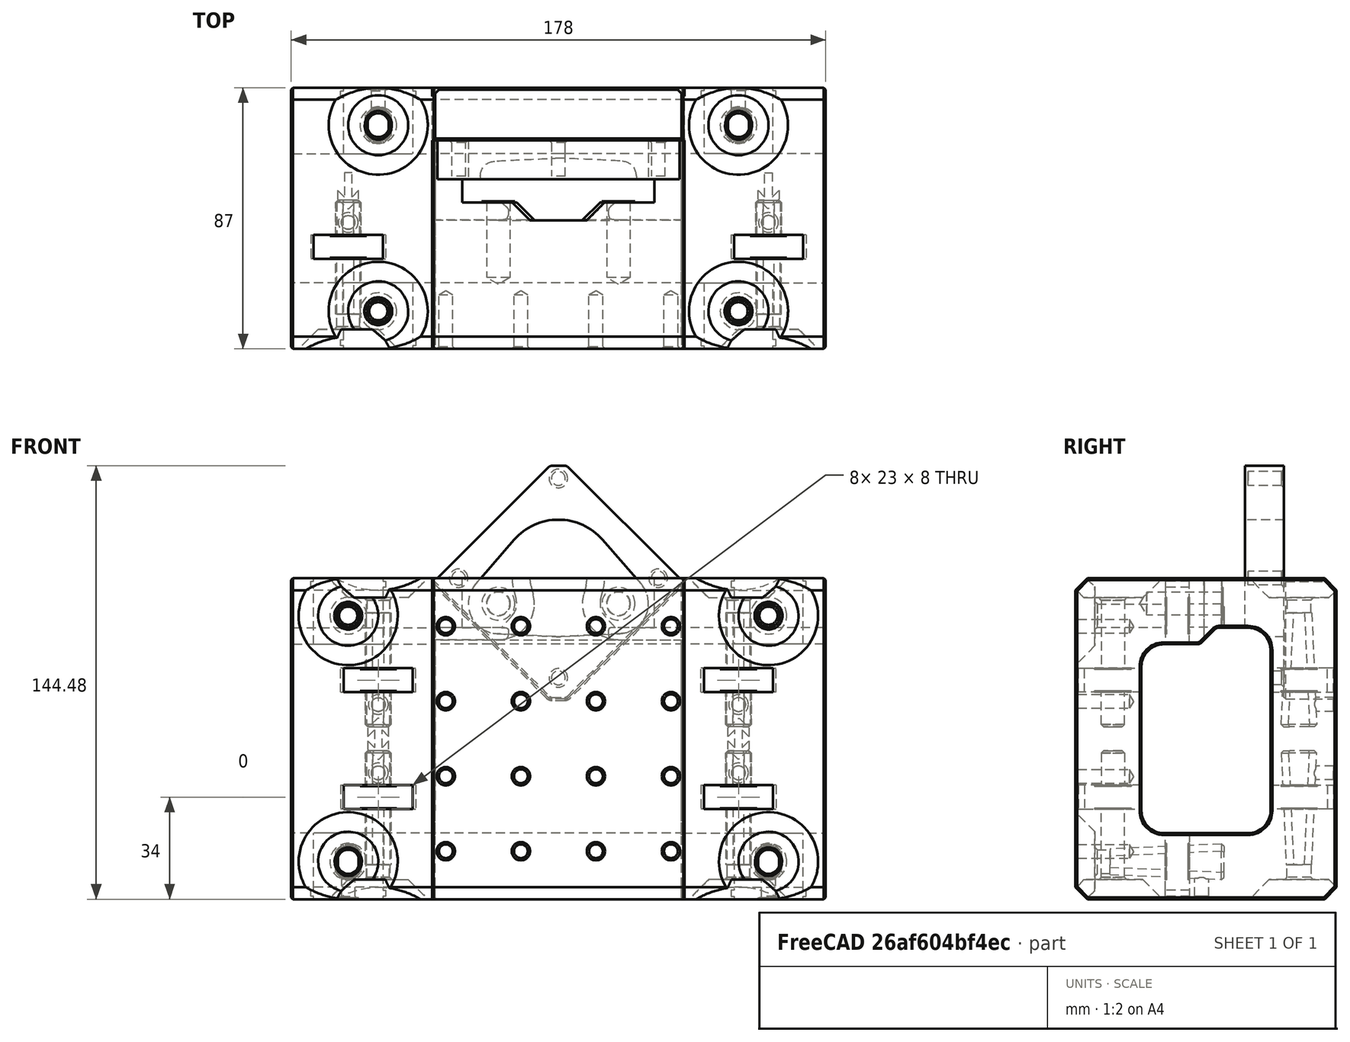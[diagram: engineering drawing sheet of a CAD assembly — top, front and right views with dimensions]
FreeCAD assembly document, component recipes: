
FREECAD ASSEMBLY — COMPONENT RECIPES ("Fabricatable-Axis-6.01-60mmx40mm-tube-version-Belt-drive-assembly")

This assembly document has 4 components, labeled P0..P3 below (a component is one placed body or linked part). 2 of them carry a construction recipe — the FreeCAD feature program that regenerates the part from scratch, quoted from this document or its linked companion documents; the rest are supplied as boundary geometry only. No exploded tour is included for this assembly.
COMPONENT P0 — recipe-attached ("Bearing ring - with all booleans", a linked part whose construction recipe lives in a companion FreeCAD document of the same project; that document's serialized recipe follows).
Construction recipe (the companion document, serialized — sketch geometry with constraints, then the solid features built on it; lengths are millimeters unless a unit is written):

FCSTD DOCUMENT  (FreeCAD 1.0R38641 +678 (Git))
Label: Fabricatable-Axis-6.01-60mmx40mm-tube-version-Bearing-ring
License: Creative Commons Attribution-ShareAlike 4.0
LicenseURL: https://creativecommons.org/licenses/by-sa/4.0/
objects: Part::FeaturePython×17, Sketcher::SketchObject×16, PartDesign::Pad×14, PartDesign::Body×9, PartDesign::Chamfer×7, PartDesign::Fillet×4, Part::Cut×3, App::Part×2, PartDesign::Pocket×2, Part::MultiFuse×2, Part::Compound×2, App::VarSet×1, PartDesign::Thickness×1, PartDesign::LinearPattern×1, PartDesign::FeatureBase×1
note: 153 computed .brp shape members not serialized (recipe doc carries the construction recipe); baked Part::Feature solids carry a one-line shape summary decoded from their .brp

FEATURE [App::VarSet] VarSet
  Attachment_hole_distance_from_edge = 8
  Attachment_hole_self_tap_diameter = 4.6
  Attachment_hole_spacing_horizontal = 60
  Attachment_hole_spacing_vertical = 80
  Bearing_axel_screw_oval_hole_depth = 5
  Bearing_axle_screw_diameter = 8
  Bearing_axle_screw_diameter_loose_diamter = 8.5
  Bearing_axle_screw_diameter_oval_selftap_diameter = 7.5
  Bearing_axle_screw_head_pocket_depth = 6.5
  Bearing_axle_screw_head_pocket_diamter = 20
  Bearing_axle_screw_length = 40
  Bearing_axle_screw_selftap_diameter = 7.7
  Bearing_distance_from_edge = 8
  Bearing_distance_from_fillet = 1
  Bearing_id = 8
  Bearing_od = 22
  Bearing_slot_width_margin = 1
  Bearing_tuning_screw_selftap_diameter = 4.6
  Bearing_washer_protrusion = 0.36
  Bearing_width = 7
  Carriage_to_bearing_top_clearance = 1.5
  Carriage_to_tube_clearance = 1.5
  Drive_chain_slot_height = 7
  Drive_chain_slot_width = 18
  Pivot_joint_spacer_thickness = 1.2
  Screw_offset = 2
  Tube_fillet_radius = 6
  Tube_height = 60
  Tube_thickness = 3
  Tube_width = 40
  Tuning_range_bearing = 2
FEATURE [Sketcher::SketchObject] Sketch
  ArcFitTolerance = 1e-06
  AttachmentSupport = -> [YZ_Plane]
  FullyConstrained = true
  MakeInternals = false
  MapMode = 5
  Placement = pos=(0,0,0) rot=(0.57735,0.57735,0.57735;2.0944rad)
  expr: .Constraints.beamheight = VarSet.Tube_height
  expr: .Constraints.beamwidth = VarSet.Tube_width
  sketch-geometry (4):
    g0: LineSegment StartX=-20 StartY=-30 StartZ=0 EndX=20 EndY=-30 EndZ=0
    g1: LineSegment StartX=20 StartY=-30 StartZ=0 EndX=20 EndY=30 EndZ=0
    g2: LineSegment StartX=20 StartY=30 StartZ=0 EndX=-20 EndY=30 EndZ=0
    g3: LineSegment StartX=-20 StartY=30 StartZ=0 EndX=-20 EndY=-30 EndZ=0
  constraints (10):
    c: Horizontal(g2)
    c: Vertical(g3)
    c: Distance(g1,g3) = 40  'beamwidth'
    c: Distance(g0,g2) = 60  'beamheight'
    c: Coincident(g0,g1)
    c: Coincident(g2,g1)
    c: Coincident(g3,g0)
    c: Coincident(g2,g3)
    c: Symmetric(g0,g1,g-1)
    c: Symmetric(g0,g0,g-2)
FEATURE [PartDesign::Pad] Pad
  Direction = (1,0,0)
  Length = 250
  Length2 = 10
  Midplane = true
  Placement = pos=(0,0,0) rot=(1,1,1;2.0944rad)
  Profile = -> Sketch
  ReferenceAxis = -> Sketch [N_Axis]
  Refine = true
  Reversed = true
  Suppressed = false
  Type = 0
FEATURE [PartDesign::Fillet] Fillet
  Base = -> Pad [Edge5,Edge2,Edge8,Edge1]
  BaseFeature = -> Pad
  Placement = pos=(0,0,0) rot=(1,1,1;2.0944rad)
  Radius = 6
  Refine = true
  SupportTransform = false
  Suppressed = false
  UseAllEdges = false
  expr: Radius = VarSet.Tube_fillet_radius
FEATURE [PartDesign::Thickness] Thickness
  Base = -> Fillet [Face2,Face5]
  BaseFeature = -> Fillet
  Intersection = false
  Join = 0
  Mode = 0
  Refine = true
  Reversed = true
  SupportTransform = false
  Suppressed = false
  Value = 3
  expr: Value = VarSet.Tube_thickness
FEATURE [PartDesign::Body] Body  label="Steel tube"
  AllowCompound = false
  Group = -> [Sketch,Pad,Fillet,Thickness]
  Origin = -> Origin
  Tip = -> Thickness
FEATURE [Sketcher::SketchObject] Sketch002
  ArcFitTolerance = 1e-06
  AttachmentSupport = -> [XY_Plane001]
  FullyConstrained = true
  MakeInternals = false
  MapMode = 5
  expr: Constraints[2] = VarSet.Bearing_od
  expr: Constraints[3] = VarSet.Bearing_id
  sketch-geometry (2):
    g0: Circle CenterX=0 CenterY=0 CenterZ=0 NormalX=0 NormalY=0 NormalZ=1 AngleXU=0 Radius=11
    g1: Circle CenterX=0 CenterY=0 CenterZ=0 NormalX=0 NormalY=0 NormalZ=1 AngleXU=0 Radius=4
  constraints (4):
    c: Coincident(g0,g-1)
    c: Coincident(g1,g0)
    c: Diameter(g0) = 22
    c: Diameter(g1) = 8
FEATURE [PartDesign::Pad] Pad001
  Direction = (0,0,1)
  Length = 7
  Length2 = 10
  Midplane = true
  Profile = -> Sketch002
  ReferenceAxis = -> Sketch002 [N_Axis]
  Refine = true
  Suppressed = false
  Type = 0
  expr: Length = VarSet.Bearing_width
FEATURE [Sketcher::SketchObject] Sketch003
  ArcFitTolerance = 1e-06
  AttachmentSupport = -> [YZ_Plane006]
  FullyConstrained = true
  MakeInternals = false
  MapMode = 5
  Placement = pos=(0,0,0) rot=(0.57735,0.57735,0.57735;2.0944rad)
  expr: .Constraints.y = VarSet.Tube_width / 2 + VarSet.Carriage_to_tube_clearance
  expr: .Constraints.z = VarSet.Tube_height / 2 + VarSet.Carriage_to_tube_clearance
  expr: Constraints[22] = VarSet.Tube_height / 2 + VarSet.Carriage_to_bearing_top_clearance + VarSet.Bearing_od
  expr: Constraints[23] = VarSet.Tube_width / 2 + VarSet.Carriage_to_bearing_top_clearance + VarSet.Bearing_od
  sketch-geometry (10):
    g0: LineSegment StartX=21.5 StartY=-31.5 StartZ=0 EndX=21.5 EndY=31.5 EndZ=0
    g1: LineSegment StartX=21.5 StartY=31.5 StartZ=0 EndX=-21.5 EndY=31.5 EndZ=0
    g2: LineSegment StartX=-21.5 StartY=31.5 StartZ=0 EndX=-21.5 EndY=-31.5 EndZ=0
    g3: LineSegment StartX=-21.5 StartY=-31.5 StartZ=0 EndX=21.5 EndY=-31.5 EndZ=0
    g4: GeomPoint [constr] X=0 Y=0 Z=0
    g5: LineSegment StartX=43.5 StartY=-53.5 StartZ=0 EndX=43.5 EndY=53.5 EndZ=0
    g6: LineSegment StartX=43.5 StartY=53.5 StartZ=0 EndX=-43.5 EndY=53.5 EndZ=0
    g7: LineSegment StartX=-43.5 StartY=53.5 StartZ=0 EndX=-43.5 EndY=-53.5 EndZ=0
    g8: LineSegment StartX=-43.5 StartY=-53.5 StartZ=0 EndX=43.5 EndY=-53.5 EndZ=0
    g9: GeomPoint [constr] X=0 Y=0 Z=0
  constraints (24):
    c: Coincident(g0,g1)
    c: Coincident(g1,g2)
    c: Coincident(g2,g3)
    c: Coincident(g3,g0)
    c: Vertical(g0)
    c: Vertical(g2)
    c: Horizontal(g1)
    c: Horizontal(g3)
    c: Symmetric(g2,g0,g4)
    c: Coincident(g4,g-1)
    c: Coincident(g5,g6)
    c: Coincident(g6,g7)
    c: Coincident(g7,g8)
    c: Coincident(g8,g5)
    c: Vertical(g5)
    c: Vertical(g7)
    c: Horizontal(g6)
    c: Horizontal(g8)
    c: Symmetric(g7,g5,g9)
    c: Coincident(g9,g4)
    c: DistanceY(g-1,g0) = 31.5  'z'
    c: DistanceX(g-2,g0) = 21.5  'y'
    c: DistanceY(g-1,g5) = 53.5
    c: DistanceX(g-2,g5) = 43.5
FEATURE [PartDesign::Fillet] Fillet001
  Base = -> Pad001 [Face3,Face4]
  BaseFeature = -> Pad001
  Radius = 0.5
  Refine = true
  SupportTransform = false
  Suppressed = false
  UseAllEdges = false
FEATURE [PartDesign::Body] Body001  label="Bearing"
  AllowCompound = false
  Group = -> [Sketch002,Pad001,Fillet001]
  Origin = -> Origin001
  Tip = -> Fillet001
FEATURE [Part::FeaturePython] Clone  label="Bearing001"  # Draft clone (typed FeaturePython)
  AttacherType = Attacher::AttachEngine3D
  Fuse = false
  Objects = -> [Body001]
  Placement = pos=(-5,-31,-19.5) rot=(0,0,1;0rad)
  Scale = (1,1,1)
  expr: .Placement.Base.x = -VarSet.Bearing_axle_screw_diameter / 2 - VarSet.Screw_offset / 2
  expr: .Placement.Base.y = -VarSet.Tube_width / 2 - VarSet.Bearing_od / 2
  expr: .Placement.Base.z = -VarSet.Tube_height / 2 + VarSet.Tube_fillet_radius + VarSet.Bearing_width / 2 + VarSet.Bearing_distance_from_fillet
FEATURE [Part::FeaturePython] Clone001  label="Bearing002"  # Draft clone (typed FeaturePython)
  AttacherType = Attacher::AttachEngine3D
  Fuse = false
  Objects = -> [Body001]
  Placement = pos=(-5,-31,19.5) rot=(0,0,1;0rad)
  Scale = (1,1,1)
  expr: .Placement.Base.x = <<Bearing001>>.Placement.Base.x
  expr: .Placement.Base.y = <<Bearing001>>.Placement.Base.y
  expr: .Placement.Base.z = -<<Bearing001>>.Placement.Base.z
FEATURE [Part::FeaturePython] Clone002  label="Bearing003"  # Draft clone (typed FeaturePython)
  AttacherType = Attacher::AttachEngine3D
  Fuse = false
  Objects = -> [Body001]
  Placement = pos=(-5,31,-19.5) rot=(0,0,1;0rad)
  Scale = (1,1,1)
  expr: .Placement.Base.x = <<Bearing001>>.Placement.Base.x
  expr: .Placement.Base.y = -<<Bearing001>>.Placement.Base.y
  expr: .Placement.Base.z = <<Bearing001>>.Placement.Base.z
FEATURE [Part::FeaturePython] Clone003  label="Bearing004"  # Draft clone (typed FeaturePython)
  AttacherType = Attacher::AttachEngine3D
  Fuse = false
  Objects = -> [Body001]
  Placement = pos=(-5,31,19.5) rot=(0,0,1;0rad)
  Scale = (1,1,1)
  expr: .Placement.Base.x = <<Bearing001>>.Placement.Base.x
  expr: .Placement.Base.y = -<<Bearing001>>.Placement.Base.y
  expr: .Placement.Base.z = -<<Bearing001>>.Placement.Base.z
FEATURE [Part::FeaturePython] Clone004  label="Bearing005"  # Draft clone (typed FeaturePython)
  AttacherType = Attacher::AttachEngine3D
  Fuse = false
  Objects = -> [Body001]
  Placement = pos=(5,-9.5,-41) rot=(1,0,0;1.5708rad)
  Scale = (1,1,1)
  expr: .Placement.Base.x = +VarSet.Bearing_axle_screw_diameter / 2 + VarSet.Screw_offset / 2
  expr: .Placement.Base.y = -VarSet.Tube_width / 2 + VarSet.Tube_fillet_radius + VarSet.Bearing_width / 2 + VarSet.Bearing_distance_from_fillet
  expr: .Placement.Base.z = -VarSet.Tube_height / 2 - VarSet.Bearing_od / 2
FEATURE [Part::FeaturePython] Clone005  label="Bearing006"  # Draft clone (typed FeaturePython)
  AttacherType = Attacher::AttachEngine3D
  Fuse = false
  Objects = -> [Body001]
  Placement = pos=(5,-9.5,41) rot=(1,0,0;4.71239rad)
  Scale = (1,1,1)
  expr: .Placement.Base.x = <<Bearing005>>.Placement.Base.x
  expr: .Placement.Base.y = -VarSet.Tube_width / 2 + VarSet.Tube_fillet_radius + VarSet.Bearing_width / 2 + VarSet.Bearing_distance_from_fillet
  expr: .Placement.Base.z = -<<Bearing005>>.Placement.Base.z
FEATURE [App::Part] Part001  label="Bearings"
  Group = -> [Body001,Clone,Clone001,Clone002,Clone003,Clone004,Clone005]
  Origin = -> Origin005
FEATURE [PartDesign::Pad] Pad002
  Direction = (1,0,0)
  Length = 48
  Length2 = 10
  Midplane = true
  Placement = pos=(0,0,0) rot=(1,1,1;2.0944rad)
  Profile = -> Sketch003
  ReferenceAxis = -> Sketch003 [N_Axis]
  Refine = true
  Suppressed = false
  Type = 0
  expr: Length = VarSet.Bearing_axle_screw_diameter + VarSet.Screw_offset + VarSet.Bearing_od + VarSet.Bearing_distance_from_edge * 2
FEATURE [Part::FeaturePython] Screw001  label="M5x10-Screw"  # WARN: FeaturePython — macro-defined, semantics opaque (R4)
  Diameter = 8
  Invert = false
  LeftHanded = false
  Length = 3
  LengthCustom = 10
  MatchOuter = false
  OffsetAngle = 0
  Placement = pos=(34,-50,30) rot=(1,0,0;1.5708rad)
  Thread = false
  Type = 70
FEATURE [Sketcher::SketchObject] Sketch005
  ArcFitTolerance = 1e-06
  AttachmentSupport = -> [XY_Plane008]
  FullyConstrained = true
  MakeInternals = false
  MapMode = 5
  expr: Constraints[11] = -VarSet.Bearing_od / 2 - VarSet.Carriage_to_bearing_top_clearance
  expr: Constraints[31] = VarSet.Bearing_slot_width_margin + VarSet.Bearing_od + 2 mm
  expr: Constraints[32] = -VarSet.Bearing_od / 2 - VarSet.Carriage_to_bearing_top_clearance + 1 mm
  expr: Constraints[33] = -VarSet.Bearing_od / 2 - VarSet.Carriage_to_bearing_top_clearance + 3 mm
  expr: Constraints[8] = VarSet.Bearing_slot_width_margin + VarSet.Bearing_od
  expr: Constraints[9] = VarSet.Bearing_od / 2
  sketch-geometry (13):
    g0: LineSegment StartX=11.5 StartY=-12.5 StartZ=0 EndX=11.5 EndY=11 EndZ=0
    g1: LineSegment StartX=11.5 StartY=11 StartZ=0 EndX=-11.5 EndY=11 EndZ=0
    g2: LineSegment StartX=-11.5 StartY=11 StartZ=0 EndX=-11.5 EndY=-12.5 EndZ=0
    g3: LineSegment StartX=-11.5 StartY=-12.5 StartZ=0 EndX=11.5 EndY=-12.5 EndZ=0
    g4: GeomPoint [constr] X=0 Y=0 Z=0
    g5: LineSegment StartX=11.5 StartY=-11.5 StartZ=0 EndX=12.5 EndY=-11.5 EndZ=0
    g6: LineSegment StartX=12.5 StartY=-11.5 StartZ=0 EndX=12.5 EndY=-9.5 EndZ=0
    g7: LineSegment StartX=12.5 StartY=-9.5 StartZ=0 EndX=11.5 EndY=-9.5 EndZ=0
    g8: LineSegment StartX=11.5 StartY=-9.5 StartZ=0 EndX=11.5 EndY=-11.5 EndZ=0
    g9: LineSegment StartX=-11.5 StartY=-9.5 StartZ=0 EndX=-12.5 EndY=-9.5 EndZ=0
    g10: LineSegment StartX=-12.5 StartY=-9.5 StartZ=0 EndX=-12.5 EndY=-11.5 EndZ=0
    g11: LineSegment StartX=-12.5 StartY=-11.5 StartZ=0 EndX=-11.5 EndY=-11.5 EndZ=0
    g12: LineSegment StartX=-11.5 StartY=-11.5 StartZ=0 EndX=-11.5 EndY=-9.5 EndZ=0
  constraints (34):
    c: Coincident(g0,g1)
    c: Coincident(g1,g2)
    c: Coincident(g2,g3)
    c: Coincident(g3,g0)
    c: Vertical(g0)
    c: Vertical(g2)
    c: Horizontal(g1)
    c: Coincident(g4,g-1)
    c: Distance(g3) = 23
    c: DistanceY(g-1,g0) = 11
    c: Symmetric(g0,g2,g-2)
    c: DistanceY(g-1,g0) = -12.5
    c: Coincident(g5,g6)
    c: Coincident(g6,g7)
    c: Coincident(g7,g8)
    c: Coincident(g8,g5)
    c: Horizontal(g5)
    c: Horizontal(g7)
    c: Vertical(g6)
    c: Vertical(g8)
    c: PointOnObject(g5,g0)
    c: Coincident(g9,g10)
    c: Coincident(g10,g11)
    c: Coincident(g11,g12)
    c: Coincident(g12,g9)
    c: Horizontal(g9)
    c: Horizontal(g11)
    c: Vertical(g10)
    c: Vertical(g12)
    c: Symmetric(g9,g7,g-2)
    c: Symmetric(g10,g5,g-2)
    c: Distance(g5,g10) = 25
    c: DistanceY(g-1,g5) = -11.5
    c: DistanceY(g-1,g6) = -9.5
FEATURE [Sketcher::SketchObject] Sketch006
  ArcFitTolerance = 1e-06
  AttachmentSupport = -> [YZ_Plane006]
  FullyConstrained = true
  MakeInternals = false
  MapMode = 5
  Placement = pos=(0,0,0) rot=(0.57735,0.57735,0.57735;2.0944rad)
  expr: Constraints[10] = Sketch003.Constraints.y - VarSet.Drive_chain_slot_width
  expr: Constraints[7] = Sketch003.Constraints.y
  expr: Constraints[8] = Sketch003.Constraints.z
  expr: Constraints[9] = VarSet.Tube_height / 2 + VarSet.Drive_chain_slot_height
  sketch-geometry (4):
    g0: LineSegment StartX=-2 StartY=31.5 StartZ=0 EndX=21.5 EndY=31.5 EndZ=0
    g1: LineSegment StartX=21.5 StartY=31.5 StartZ=0 EndX=21.5 EndY=37 EndZ=0
    g2: LineSegment StartX=21.5 StartY=37 StartZ=0 EndX=3.5 EndY=37 EndZ=0
    g3: LineSegment StartX=3.5 StartY=37 StartZ=0 EndX=-2 EndY=31.5 EndZ=0
  constraints (12):
    c: Coincident(g0,g1)
    c: Coincident(g1,g2)
    c: Coincident(g2,g3)
    c: Coincident(g3,g0)
    c: Horizontal(g0)
    c: Horizontal(g2)
    c: Vertical(g1)
    c: DistanceX(g-2,g0) = 21.5
    c: DistanceY(g-1,g0) = 31.5
    c: DistanceY(g-1,g1) = 37
    c: DistanceX(g-2,g2) = 3.5
    c: Angle(g-2,g3) = 2.35619
FEATURE [PartDesign::Pocket] Pocket
  BaseFeature = -> Pad002
  Direction = (-1,0,0)
  Length = 5
  Length2 = 5
  Midplane = true
  Placement = pos=(0,0,0) rot=(1,1,1;2.0944rad)
  Profile = -> Sketch006
  ReferenceAxis = -> Sketch006 [N_Axis]
  Refine = true
  Suppressed = false
  Type = 1
FEATURE [PartDesign::Fillet] Fillet006
  Base = -> Pocket [Edge26,Edge30,Edge29,Edge28]
  BaseFeature = -> Pocket
  Placement = pos=(0,0,0) rot=(1,1,1;2.0944rad)
  Radius = 7.5
  Refine = true
  SupportTransform = false
  Suppressed = false
  UseAllEdges = false
  expr: Radius = VarSet.Tube_fillet_radius + VarSet.Carriage_to_tube_clearance
FEATURE [PartDesign::Fillet] Fillet007
  Base = -> Fillet006 [Edge25,Edge29]
  BaseFeature = -> Fillet006
  Placement = pos=(0,0,0) rot=(1,1,1;2.0944rad)
  Radius = 2
  Refine = true
  SupportTransform = false
  Suppressed = false
  UseAllEdges = false
FEATURE [PartDesign::Chamfer] Chamfer
  Angle = 45
  Base = -> Fillet007 [Edge44,Edge46,Edge41,Edge42]
  BaseFeature = -> Fillet007
  ChamferType = 0
  FlipDirection = false
  Placement = pos=(0,0,0) rot=(1,1,1;2.0944rad)
  Refine = true
  Size = 4
  Size2 = 1
  SupportTransform = false
  Suppressed = false
  UseAllEdges = false
FEATURE [PartDesign::Pad] Pad004
  Direction = (0,0,1)
  Length = 8
  Length2 = 10
  Midplane = true
  Profile = -> Sketch005
  ReferenceAxis = -> Sketch005 [N_Axis]
  Refine = true
  Suppressed = false
  Type = 0
  expr: Length = VarSet.Bearing_width + VarSet.Bearing_slot_width_margin
FEATURE [Sketcher::SketchObject] Sketch007
  ArcFitTolerance = 1e-06
  AttachmentOffset = pos=(0,0,4) rot=(0,0,1;0rad)
  AttachmentSupport = -> [XY_Plane008]
  FullyConstrained = true
  MakeInternals = false
  MapMode = 5
  Placement = pos=(0,0,4) rot=(0,0,1;0rad)
  expr: .AttachmentOffset.Base.z = Pad004.Length / 2
  expr: Constraints[1] = VarSet.Bearing_od / 1.8
  sketch-geometry (1):
    g0: Circle CenterX=0 CenterY=0 CenterZ=0 NormalX=0 NormalY=0 NormalZ=1 AngleXU=0 Radius=6.11111
  constraints (2):
    c: Coincident(g0,g-1)
    c: Diameter(g0) = 12.2222
FEATURE [PartDesign::Pocket] Pocket001
  BaseFeature = -> Pad004
  Direction = (0,0,-1)
  Length = 0.36
  Length2 = 5
  Profile = -> Sketch007
  ReferenceAxis = -> Sketch007 [N_Axis]
  Refine = true
  Suppressed = false
  Type = 0
  expr: Length = VarSet.Bearing_washer_protrusion
FEATURE [PartDesign::LinearPattern] LinearPattern
  BaseFeature = -> Pocket001
  Direction = -> Z_Axis008
  Length = 7.64
  Mode = 0
  Occurrences = 2
  Offset = 7.64
  Originals = -> [Pocket001]
  Refine = true
  Reversed = true
  Suppressed = false
  TransformMode = 0
  expr: Length = Pad004.Length - Pocket001.Length
FEATURE [PartDesign::FeatureBase] Clone007
  BaseFeature = -> LinearPattern
  Suppressed = false
FEATURE [PartDesign::Body] Body005  label="Body for boolean - hole maker adjustable"
  AllowCompound = false
  Group = -> [Clone007]
  Origin = -> Origin009
  Tip = -> Clone007
FEATURE [Sketcher::SketchObject] Sketch008
  ArcFitTolerance = 1e-06
  AttachmentSupport = -> [XY_Plane008]
  FullyConstrained = true
  MakeInternals = false
  MapMode = 5
  expr: Constraints[1] = VarSet.Bearing_axle_screw_selftap_diameter
  sketch-geometry (1):
    g0: Circle CenterX=0 CenterY=0 CenterZ=0 NormalX=0 NormalY=0 NormalZ=1 AngleXU=0 Radius=3.85
  constraints (2):
    c: Coincident(g0,g-1)
    c: Diameter(g0) = 7.7
FEATURE [PartDesign::Pad] Pad005
  BaseFeature = -> LinearPattern
  Direction = (0,0,1)
  Length = 27.5
  Length2 = 10
  Profile = -> Sketch008
  ReferenceAxis = -> Sketch008 [N_Axis]
  Refine = true
  Suppressed = false
  Type = 0
  expr: Length = VarSet.Bearing_width / 2 + VarSet.Bearing_distance_from_fillet + VarSet.Tube_fillet_radius + VarSet.Bearing_od + VarSet.Carriage_to_bearing_top_clearance - VarSet.Bearing_axle_screw_head_pocket_depth
FEATURE [PartDesign::Pad] Pad006
  BaseFeature = -> Pad005
  Direction = (0,0,1)
  Length = 15.5
  Length2 = 10
  Profile = -> Sketch008
  ReferenceAxis = -> Sketch008 [N_Axis]
  Refine = true
  Reversed = true
  Suppressed = false
  Type = 0
  expr: Length = VarSet.Bearing_axle_screw_length + 3 mm - Pad005.Length
FEATURE [Sketcher::SketchObject] Sketch009
  ArcFitTolerance = 1e-06
  AttachmentSupport = -> [Pad006]
  FullyConstrained = true
  MakeInternals = false
  MapMode = 5
  Placement = pos=(0,0,27.5) rot=(0,0,1;0rad)
  expr: Constraints[1] = VarSet.Bearing_axle_screw_head_pocket_diamter
  sketch-geometry (1):
    g0: Circle CenterX=0 CenterY=0 CenterZ=0 NormalX=0 NormalY=0 NormalZ=1 AngleXU=0 Radius=10
  constraints (2):
    c: Coincident(g0,g-1)
    c: Diameter(g0) = 20
FEATURE [PartDesign::Pad] Pad007
  BaseFeature = -> Pad006
  Direction = (0,0,1)
  Length = 6.5
  Length2 = 10
  Profile = -> Sketch009
  ReferenceAxis = -> Sketch009 [N_Axis]
  Refine = true
  Suppressed = false
  TaperAngle = 45
  Type = 0
  expr: Length = VarSet.Bearing_axle_screw_head_pocket_depth
FEATURE [PartDesign::Chamfer] Chamfer002
  Angle = 45
  Base = -> Pad007 [Edge46,Edge48]
  BaseFeature = -> Pad007
  ChamferType = 0
  FlipDirection = false
  Refine = true
  Size = 0.8
  Size2 = 1
  SupportTransform = false
  Suppressed = false
  UseAllEdges = false
FEATURE [PartDesign::Chamfer] Chamfer003
  Angle = 45
  Base = -> Chamfer002 [Edge51,Edge3]
  BaseFeature = -> Chamfer002
  ChamferType = 0
  FlipDirection = false
  Refine = true
  Size = 0.3
  Size2 = 1
  SupportTransform = false
  Suppressed = false
  UseAllEdges = false
FEATURE [PartDesign::Body] Body004  label="Body - hole maker non adjustable"
  AllowCompound = false
  Group = -> [Sketch005,Pad004,Sketch007,Pocket001,LinearPattern,Sketch008,Pad005,Pad006,Sketch009,Pad007,Chamfer002,Chamfer003]
  Origin = -> Origin008
  Tip = -> Chamfer003
FEATURE [Part::FeaturePython] Clone006  label="Clone - hole maker non adjustable - for bearing002"  # Draft clone (typed FeaturePython)
  AttacherType = Attacher::AttachEngine3D
  Fuse = false
  Objects = -> [Body004]
  Placement = pos=(-5,-31,19.5) rot=(0,0,1;0rad)
  Scale = (1,1,1)
  expr: .Placement.Base.x = <<Bearing002>>.Placement.Base.x
  expr: .Placement.Base.y = <<Bearing002>>.Placement.Base.y
  expr: .Placement.Base.z = <<Bearing002>>.Placement.Base.z
FEATURE [Part::FeaturePython] Clone008  label="Clone - hole maker non adjustable - for bearing006"  # Draft clone (typed FeaturePython)
  AttacherType = Attacher::AttachEngine3D
  Fuse = false
  Objects = -> [Body004]
  Placement = pos=(5,-9.5,41) rot=(0,-0.707107,0.707107;3.14159rad)
  Scale = (1,1,1)
  expr: .Placement.Base.x = <<Bearing006>>.Placement.Base.x
  expr: .Placement.Base.y = <<Bearing006>>.Placement.Base.y
  expr: .Placement.Base.z = <<Bearing006>>.Placement.Base.z
FEATURE [Sketcher::SketchObject] Sketch013
  ArcFitTolerance = 1e-06
  AttachmentSupport = -> [YZ_Plane011]
  FullyConstrained = true
  MakeInternals = false
  MapMode = 5
  Placement = pos=(0,0,0) rot=(0.57735,0.57735,0.57735;2.0944rad)
  expr: .Constraints.z = Pad005.Length - VarSet.Bearing_axel_screw_oval_hole_depth
  expr: Constraints[12] = VarSet.Bearing_axle_screw_diameter_loose_diamter + VarSet.Tuning_range_bearing
  expr: Constraints[7] = -Pad006.Length
  expr: Constraints[8] = VarSet.Bearing_axle_screw_diameter_loose_diamter
  sketch-geometry (5):
    g0: LineSegment StartX=-4.25 StartY=22.5 StartZ=0 EndX=-5.93889 EndY=-15.5 EndZ=0
    g1: LineSegment StartX=-5.93889 StartY=-15.5 StartZ=0 EndX=5.93889 EndY=-15.5 EndZ=0
    g2: LineSegment StartX=5.93889 StartY=-15.5 StartZ=0 EndX=4.25 EndY=22.5 EndZ=0
    g3: LineSegment StartX=4.25 StartY=22.5 StartZ=0 EndX=-4.25 EndY=22.5 EndZ=0
    g4: LineSegment [constr] StartX=-5.25 StartY=0 StartZ=0 EndX=5.25 EndY=0 EndZ=0
  constraints (14):
    c: Coincident(g0,g1)
    c: Coincident(g1,g2)
    c: Coincident(g2,g3)
    c: Coincident(g3,g0)
    c: Symmetric(g2,g0,g-2)
    c: Symmetric(g0,g1,g-2)
    c: DistanceY(g-1,g2) = 22.5  'z'
    c: DistanceY(g-1,g1) = -15.5
    c: Distance(g3) = 8.5
    c: Distance(g1) = 11.8778
    c: PointOnObject(g4,g-1)
    c: Symmetric(g4,g4,g-2)
    c: Distance(g4) = 10.5
    c: PointOnObject(g4,g0)
FEATURE [PartDesign::Pad] Pad008
  Direction = (1,0,0)
  Length = 8.5
  Length2 = 10
  Midplane = true
  Placement = pos=(0,0,0) rot=(1,1,1;2.0944rad)
  Profile = -> Sketch013
  ReferenceAxis = -> Sketch013 [N_Axis]
  Refine = true
  Suppressed = false
  Type = 0
  expr: Length = VarSet.Bearing_axle_screw_diameter_loose_diamter
FEATURE [PartDesign::Chamfer] Chamfer004
  Angle = 45
  Base = -> Pad008 [Edge4,Edge3,Edge10,Edge9]
  BaseFeature = -> Pad008
  ChamferType = 0
  FlipDirection = false
  Placement = pos=(0,0,0) rot=(1,1,1;2.0944rad)
  Refine = true
  Size = 2.42857
  Size2 = 1
  SupportTransform = false
  Suppressed = false
  UseAllEdges = false
  expr: Size = VarSet.Bearing_axle_screw_diameter_loose_diamter / 3.5
FEATURE [PartDesign::Chamfer] Chamfer005
  Angle = 45
  Base = -> Chamfer004 [Face5]
  BaseFeature = -> Chamfer004
  ChamferType = 0
  FlipDirection = false
  Placement = pos=(0,0,0) rot=(1,1,1;2.0944rad)
  Refine = true
  Size = 0.8
  Size2 = 1
  SupportTransform = false
  Suppressed = false
  UseAllEdges = false
FEATURE [Sketcher::SketchObject] Sketch014
  ArcFitTolerance = 1e-06
  AttachmentOffset = pos=(0,0,22.5) rot=(0,0,1;0rad)
  AttachmentSupport = -> [XY_Plane011]
  FullyConstrained = false
  MakeInternals = false
  MapMode = 5
  Placement = pos=(0,0,22.5) rot=(0,0,1;0rad)
  expr: .AttachmentOffset.Base.z = Sketch013.Constraints.z
  expr: Constraints[5] = VarSet.Bearing_axle_screw_diameter
  expr: Constraints[6] = VarSet.Bearing_axle_screw_diameter_oval_selftap_diameter
  sketch-geometry (5):
    g0: Ellipse CenterX=0 CenterY=0 CenterZ=0 NormalX=0 NormalY=0 NormalZ=1 MajorRadius=4 MinorRadius=3.75 AngleXU=-1.5708
    g1: LineSegment [constr] StartX=1e-16 StartY=-4 StartZ=0 EndX=-1e-16 EndY=4 EndZ=0
    g2: LineSegment [constr] StartX=3.75 StartY=1e-16 StartZ=0 EndX=-3.75 EndY=-1e-16 EndZ=0
    g3: GeomPoint [constr] X=2e-16 Y=-1.39194 Z=0
    g4: GeomPoint [constr] X=0 Y=1.39194 Z=0
  constraints (4):
    c: InternalAlignment(g1-g4 -> g0) x4
    c: Coincident(g0,g-1)
    c: Distance(g1,g1) = 8
    c: Distance(g2,g2) = 7.5
FEATURE [PartDesign::Pad] Pad009
  BaseFeature = -> Chamfer005
  Direction = (0,0,1)
  Length = 5
  Length2 = 10
  Placement = pos=(0,0,0) rot=(1,1,1;2.0944rad)
  Profile = -> Sketch014
  ReferenceAxis = -> Sketch014 [N_Axis]
  Refine = true
  Suppressed = false
  Type = 0
  expr: Length = VarSet.Bearing_axel_screw_oval_hole_depth
FEATURE [Sketcher::SketchObject] Sketch015
  ArcFitTolerance = 1e-06
  AttachmentOffset = pos=(0,0,27.5) rot=(0,0,1;0rad)
  AttachmentSupport = -> [XY_Plane011]
  FullyConstrained = true
  MakeInternals = false
  MapMode = 5
  Placement = pos=(0,0,27.5) rot=(0,0,1;0rad)
  expr: .AttachmentOffset.Base.z = Sketch013.Constraints.z + VarSet.Bearing_axel_screw_oval_hole_depth
  expr: Constraints[1] = VarSet.Bearing_axle_screw_head_pocket_diamter
  sketch-geometry (1):
    g0: Circle CenterX=0 CenterY=0 CenterZ=0 NormalX=0 NormalY=0 NormalZ=1 AngleXU=0 Radius=10
  constraints (2):
    c: Coincident(g0,g-1)
    c: Diameter(g0) = 20
FEATURE [PartDesign::Pad] Pad010
  BaseFeature = -> Pad009
  Direction = (0,0,1)
  Length = 32.5
  Length2 = 10
  Placement = pos=(0,0,0) rot=(1,1,1;2.0944rad)
  Profile = -> Sketch015
  ReferenceAxis = -> Sketch015 [N_Axis]
  Refine = true
  Suppressed = false
  TaperAngle = 45
  Type = 0
  expr: Length = VarSet.Bearing_axle_screw_head_pocket_depth * 5
FEATURE [Sketcher::SketchObject] Sketch016
  ArcFitTolerance = 1e-06
  AttachmentSupport = -> [XZ_Plane011]
  FullyConstrained = true
  MakeInternals = false
  MapMode = 5
  Placement = pos=(0,0,0) rot=(1,0,0;1.5708rad)
  expr: .Constraints.z = -VarSet.Bearing_width / 2 - VarSet.Bearing_slot_width_margin / 2 - VarSet.Bearing_tuning_screw_selftap_diameter / 2 - 1.8 mm
  expr: Constraints[1] = VarSet.Bearing_tuning_screw_selftap_diameter
  sketch-geometry (1):
    g0: Circle CenterX=0 CenterY=-8.1 CenterZ=0 NormalX=0 NormalY=0 NormalZ=1 AngleXU=0 Radius=2.3
  constraints (3):
    c: PointOnObject(g0,g-2)
    c: Diameter(g0) = 4.6
    c: DistanceY(g-1,g0) = -8.1  'z'
FEATURE [PartDesign::Pad] Pad011
  BaseFeature = -> Pad010
  Direction = (0,-1,2e-16)
  Length = 11.5
  Length2 = 10
  Placement = pos=(0,0,0) rot=(1,1,1;2.0944rad)
  Profile = -> Sketch016
  ReferenceAxis = -> Sketch016 [N_Axis]
  Refine = true
  Suppressed = false
  Type = 0
  expr: Length = VarSet.Bearing_od / 2 + VarSet.Carriage_to_bearing_top_clearance - 1 mm
FEATURE [Part::FeaturePython] Clone012  label="Clone - hole maker non adjustable - for bearing001"  # Draft clone (typed FeaturePython)
  AttacherType = Attacher::AttachEngine3D
  Fuse = false
  Objects = -> [Body004]
  Placement = pos=(-5,-31,-19.5) rot=(0,1,0;3.14159rad)
  Scale = (1,1,1)
  expr: .Placement.Base.x = <<Bearing001>>.Placement.Base.x
  expr: .Placement.Base.y = <<Bearing001>>.Placement.Base.y
  expr: .Placement.Base.z = <<Bearing001>>.Placement.Base.z
FEATURE [Sketcher::SketchObject] Sketch017
  ArcFitTolerance = 1e-06
  AttachmentOffset = pos=(0,0,11.5) rot=(0,0,1;0rad)
  AttachmentSupport = -> [XZ_Plane011]
  FullyConstrained = true
  MakeInternals = false
  MapMode = 5
  Placement = pos=(0,-11.5,2.6e-15) rot=(1,0,0;1.5708rad)
  expr: .AttachmentOffset.Base.z = VarSet.Bearing_od / 2 + VarSet.Carriage_to_bearing_top_clearance - 1 mm
  expr: Constraints[0] = VarSet.Bearing_tuning_screw_selftap_diameter
  expr: Constraints[1] = Sketch016.Constraints.z
  sketch-geometry (1):
    g0: Circle CenterX=0 CenterY=-8.1 CenterZ=0 NormalX=0 NormalY=0 NormalZ=1 AngleXU=0 Radius=2.3
  constraints (3):
    c: Diameter(g0) = 4.6
    c: DistanceY(g-1,g0) = -8.1
    c: PointOnObject(g0,g-2)
FEATURE [PartDesign::Pad] Pad012
  BaseFeature = -> Pad011
  Direction = (0,-1,2e-16)
  Length = 1
  Length2 = 10
  Placement = pos=(0,0,0) rot=(1,1,1;2.0944rad)
  Profile = -> Sketch017
  ReferenceAxis = -> Sketch017 [N_Axis]
  Refine = true
  Suppressed = false
  TaperAngle = 45
  Type = 0
FEATURE [PartDesign::Chamfer] Chamfer006
  Angle = 45
  Base = -> Pad012 [Edge44]
  BaseFeature = -> Pad012
  ChamferType = 0
  FlipDirection = false
  Placement = pos=(0,0,0) rot=(1,1,1;2.0944rad)
  Refine = true
  Size = 0.8
  Size2 = 1
  SupportTransform = false
  Suppressed = false
  UseAllEdges = false
FEATURE [PartDesign::Body] Body007  label="Body for boolean - rotation hole"
  AllowCompound = false
  Group = -> [Sketch013,Pad008,Chamfer004,Chamfer005,Sketch014,Pad009,Sketch015,Pad010,Sketch016,Pad011,Sketch017,Pad012,Chamfer006]
  Origin = -> Origin011
  Tip = -> Chamfer006
FEATURE [Part::MultiFuse] Fusion001  label="Fusion - hole maker adjustable"
  Refine = true
  Shapes = -> [Body005,Body007]
FEATURE [Part::FeaturePython] Clone009  label="Clone - Hole maker adjustable - for bearing003"  # Draft clone (typed FeaturePython)
  AttacherType = Attacher::AttachEngine3D
  Fuse = false
  Objects = -> [Fusion001]
  Placement = pos=(-5,31,-19.5) rot=(1,0,0;3.14159rad)
  Scale = (1,1,1)
  expr: .Placement.Base.x = <<Bearing003>>.Placement.Base.x
  expr: .Placement.Base.y = <<Bearing003>>.Placement.Base.y
  expr: .Placement.Base.z = <<Bearing003>>.Placement.Base.z
FEATURE [Part::FeaturePython] Clone010  label="Clone - Hole maker adjustable - for bearing004"  # Draft clone (typed FeaturePython)
  AttacherType = Attacher::AttachEngine3D
  Fuse = false
  Objects = -> [Fusion001]
  Placement = pos=(-5,31,19.5) rot=(0,0,1;3.14159rad)
  Scale = (1,1,1)
  expr: .Placement.Base.x = <<Bearing004>>.Placement.Base.x
  expr: .Placement.Base.y = <<Bearing004>>.Placement.Base.y
  expr: .Placement.Base.z = <<Bearing004>>.Placement.Base.z
FEATURE [Part::FeaturePython] Clone011  label="Clone - Hole maker adjustable - for bearing005"  # Draft clone (typed FeaturePython)
  AttacherType = Attacher::AttachEngine3D
  Fuse = false
  Objects = -> [Fusion001]
  Placement = pos=(5,-9.5,-41) rot=(1,0,0;1.5708rad)
  Scale = (1,1,1)
  expr: .Placement.Base.x = <<Bearing005>>.Placement.Base.x
  expr: .Placement.Base.y = <<Bearing005>>.Placement.Base.y
  expr: .Placement.Base.z = <<Bearing005>>.Placement.Base.z
FEATURE [Part::Compound] Compound  label="Hole makers- verticals"
  Links = -> [Clone006,Clone012,Clone009,Clone010]
FEATURE [Part::Compound] Compound001  label="Hole makers horizontals"
  Links = -> [Clone008,Clone011]
FEATURE [Sketcher::SketchObject] Sketch018
  ArcFitTolerance = 1e-06
  AttachmentSupport = -> [XZ_Plane012]
  FullyConstrained = false
  MakeInternals = false
  MapMode = 5
  Placement = pos=(0,0,0) rot=(1,0,0;1.5708rad)
  expr: Constraints[31] = 16
  sketch-geometry (16):
    g0: LineSegment StartX=-200 StartY=0 StartZ=0 EndX=-21 EndY=0 EndZ=0
    g1: LineSegment StartX=21 StartY=0 StartZ=0 EndX=200 EndY=0 EndZ=0
    g2: ArcOfCircle CenterX=-1e-16 CenterY=26.9798 CenterZ=0 NormalX=0 NormalY=0 NormalZ=1 AngleXU=0 Radius=8 StartAngle=1e-16 EndAngle=3.14159
    g3: ArcOfCircle CenterX=-1e-16 CenterY=26.9798 CenterZ=0 NormalX=0 NormalY=0 NormalZ=1 AngleXU=0 Radius=10 StartAngle=0 EndAngle=3.14159
    g4: ArcOfCircle CenterX=-21 CenterY=13 CenterZ=0 NormalX=0 NormalY=0 NormalZ=1 AngleXU=0 Radius=13 StartAngle=4.71239 EndAngle=6.28319
    g5: ArcOfCircle CenterX=21 CenterY=13 CenterZ=0 NormalX=0 NormalY=0 NormalZ=1 AngleXU=0 Radius=13 StartAngle=3.14159 EndAngle=4.71239
    g6: ArcOfCircle CenterX=21 CenterY=13 CenterZ=0 NormalX=0 NormalY=0 NormalZ=1 AngleXU=0 Radius=11 StartAngle=3.14159 EndAngle=4.71239
    g7: ArcOfCircle CenterX=-21 CenterY=13 CenterZ=0 NormalX=0 NormalY=0 NormalZ=1 AngleXU=0 Radius=11 StartAngle=4.71239 EndAngle=6.28319
    g8: LineSegment StartX=-200 StartY=0 StartZ=0 EndX=-200 EndY=2 EndZ=0
    g9: LineSegment StartX=-200 StartY=2 StartZ=0 EndX=-21 EndY=2 EndZ=0
    g10: LineSegment StartX=200 StartY=0 StartZ=0 EndX=200 EndY=2 EndZ=0
    g11: LineSegment StartX=200 StartY=2 StartZ=0 EndX=21 EndY=2 EndZ=0
    g12: LineSegment StartX=-10 StartY=26.9798 StartZ=0 EndX=-10 EndY=13 EndZ=0
    g13: LineSegment StartX=-8 StartY=26.9798 StartZ=0 EndX=-8 EndY=13 EndZ=0
    g14: LineSegment StartX=8 StartY=26.9798 StartZ=0 EndX=8 EndY=13 EndZ=0
    g15: LineSegment StartX=10 StartY=26.9798 StartZ=0 EndX=10 EndY=13 EndZ=0
  constraints (36):
    c: PointOnObject(g0,g-1)
    c: PointOnObject(g0,g-1)
    c: PointOnObject(g1,g-1)
    c: Coincident(g3,g2)
    c: Coincident(g6,g5)
    c: Coincident(g7,g4)
    c: Coincident(g0,g8)
    c: Vertical(g8)
    c: Coincident(g8,g9)
    c: Horizontal(g9)
    c: Coincident(g1,g10)
    c: Vertical(g10)
    c: Coincident(g10,g11)
    c: Horizontal(g11)
    c: Tangent(g1,g5) = -1.5708
    c: Tangent(g6,g11) = 1.5708
    c: Tangent(g5,g14) = -1.5708
    c: Tangent(g15,g6) = -1.5708
    c: Tangent(g15,g3) = 1.5708
    c: Tangent(g14,g2) = 1.5708
    c: Tangent(g4,g0) = -1.5708
    c: Tangent(g7,g9) = -1.5708
    c: Tangent(g7,g12) = 1.5708
    c: Tangent(g4,g13) = 1.5708
    c: Tangent(g13,g2) = -1.5708
    c: Tangent(g12,g3) = -1.5708
    c: Parallel(g12,g13)
    c: Parallel(g14,g15)
    c: Symmetric(g2,g2,g-2)
    c: Vertical(g12)
    c: Distance(g8) = 2
    c: Diameter(g2) = 16
    c: Equal(g7,g6)
    c: Diameter(g7) = 22
    c: Symmetric(g0,g1,g-2)
    c: Distance(g0,g1) = 400
FEATURE [PartDesign::Pad] Pad013
  Direction = (0,-1,2e-16)
  Length = 9
  Length2 = 10
  Placement = pos=(0,0,0) rot=(1,0,0;1.5708rad)
  Profile = -> Sketch018
  ReferenceAxis = -> Sketch018 [N_Axis]
  Refine = true
  Suppressed = false
  Type = 0
FEATURE [PartDesign::Body] Body008  label="Belt"
  AllowCompound = false
  Group = -> [Sketch018,Pad013]
  Origin = -> Origin012
  Placement = pos=(0,14,31.5) rot=(0,0,1;0rad)
  Tip = -> Pad013
  expr: .Placement.Base.y = VarSet.Tube_width / 2 - VarSet.Tube_fillet_radius
  expr: .Placement.Base.z = VarSet.Tube_height / 2 + 1.5 mm
FEATURE [Sketcher::SketchObject] Sketch019
  ArcFitTolerance = 1e-06
  AttachmentOffset = pos=(0,-12.7,12.5) rot=(0,0,1;0rad)
  AttachmentSupport = -> [XZ_Plane013]
  FullyConstrained = true
  MakeInternals = false
  MapMode = 5
  Placement = pos=(0,-12.5,-12.7) rot=(1,0,0;1.5708rad)
  expr: .AttachmentOffset.Base.y = Sketch016.Constraints.z - VarSet.Bearing_tuning_screw_selftap_diameter
  expr: .AttachmentOffset.Base.z = VarSet.Bearing_od / 2 + VarSet.Carriage_to_bearing_top_clearance
  sketch-geometry (10):
    g0: LineSegment StartX=-1.25 StartY=-12 StartZ=0 EndX=1.25 EndY=-12 EndZ=0
    g1: LineSegment StartX=1.25 StartY=-12 StartZ=0 EndX=1.25 EndY=-3.82843 EndZ=0
    g2: LineSegment StartX=1.25 StartY=-3.82843 StartZ=0 EndX=3.5 EndY=-6.07843 EndZ=0
    g3: LineSegment StartX=3.5 StartY=-6.07843 StartZ=0 EndX=3.5 EndY=-3.25 EndZ=0
    g4: LineSegment StartX=3.5 StartY=-3.25 StartZ=0 EndX=0.25 EndY=-4e-16 EndZ=0
    g5: LineSegment StartX=0.25 StartY=-4e-16 StartZ=0 EndX=-0.25 EndY=0 EndZ=0
    g6: LineSegment StartX=-0.25 StartY=0 StartZ=0 EndX=-3.5 EndY=-3.25 EndZ=0
    g7: LineSegment StartX=-3.5 StartY=-3.25 StartZ=0 EndX=-3.5 EndY=-6.07843 EndZ=0
    g8: LineSegment StartX=-3.5 StartY=-6.07843 StartZ=0 EndX=-1.25 EndY=-3.82843 EndZ=0
    g9: LineSegment StartX=-1.25 StartY=-3.82843 StartZ=0 EndX=-1.25 EndY=-12 EndZ=0
  constraints (26):
    c: Horizontal(g0)
    c: Coincident(g0,g1)
    c: Vertical(g1)
    c: Coincident(g1,g2)
    c: Coincident(g2,g3)
    c: Vertical(g3)
    c: Coincident(g3,g4)
    c: Coincident(g4,g5)
    c: Coincident(g5,g6)
    c: Coincident(g6,g7)
    c: Coincident(g7,g8)
    c: Coincident(g8,g9)
    c: Coincident(g9,g0)
    c: Vertical(g9)
    c: Symmetric(g5,g4,g-2)
    c: Symmetric(g6,g3,g-2)
    c: Symmetric(g8,g1,g-2)
    c: Symmetric(g7,g2,g-2)
    c: Distance(g5) = 0.5
    c: Parallel(g8,g6)
    c: Distance(g8,g6) = 2
    c: Distance(g0) = 2.5
    c: Angle(g8,g9) = 0.785398
    c: Distance(g7,g2) = 7
    c: PointOnObject(g4,g-1)
    c: DistanceY(g-1,g0) = -12
FEATURE [PartDesign::Pad] Pad014
  Direction = (0,-1,2e-16)
  Length = 0.5
  Length2 = 10
  Placement = pos=(0,0,0) rot=(1,0,0;1.5708rad)
  Profile = -> Sketch019
  ReferenceAxis = -> Sketch019 [N_Axis]
  Refine = true
  Reversed = true
  Suppressed = false
  Type = 0
FEATURE [PartDesign::Body] Body009  label="Tuning arrow"
  AllowCompound = false
  Group = -> [Sketch019,Pad014]
  Origin = -> Origin013
  Tip = -> Pad014
FEATURE [Part::FeaturePython] Clone013  label="Clone - Tuning arrow - for Bearing 003"  # Draft clone (typed FeaturePython)
  AttacherType = Attacher::AttachEngine3D
  Fuse = false
  Objects = -> [Body009]
  Placement = pos=(-5,31,-19.5) rot=(1,0,0;3.14159rad)
  Scale = (1,1,1)
  expr: .Placement.Base.x = <<Bearing003>>.Placement.Base.x
  expr: .Placement.Base.y = <<Bearing003>>.Placement.Base.y
  expr: .Placement.Base.z = <<Bearing003>>.Placement.Base.z
FEATURE [Part::FeaturePython] Clone014  label="Clone - Tuning arrow - for Bearing 004"  # Draft clone (typed FeaturePython)
  AttacherType = Attacher::AttachEngine3D
  Fuse = false
  Objects = -> [Body009]
  Placement = pos=(-5,31,19.5) rot=(0,0,1;3.14159rad)
  Scale = (1,1,1)
  expr: .Placement.Base.x = <<Bearing004>>.Placement.Base.x
  expr: .Placement.Base.y = <<Bearing004>>.Placement.Base.y
  expr: .Placement.Base.z = <<Bearing004>>.Placement.Base.z
FEATURE [Part::FeaturePython] Clone015  label="Clone - Tuning arrow - for Bearing 005"  # Draft clone (typed FeaturePython)
  AttacherType = Attacher::AttachEngine3D
  Fuse = false
  Objects = -> [Body009]
  Placement = pos=(5,-9.5,-41) rot=(1,0,0;1.5708rad)
  Scale = (1,1,1)
  expr: .Placement.Base.x = <<Bearing005>>.Placement.Base.x
  expr: .Placement.Base.y = <<Bearing005>>.Placement.Base.y
  expr: .Placement.Base.z = <<Bearing005>>.Placement.Base.z
FEATURE [Sketcher::SketchObject] Sketch020
  ArcFitTolerance = 1e-06
  AttachmentSupport = -> [YZ_Plane014]
  FullyConstrained = false
  MakeInternals = false
  MapMode = 5
  Placement = pos=(0,0,0) rot=(0.57735,0.57735,0.57735;2.0944rad)
  expr: Constraints[6] = VarSet.Tube_width / 2 + VarSet.Bearing_od / 2
  sketch-geometry (14):
    g0: Circle CenterX=-31 CenterY=16 CenterZ=0 NormalX=0 NormalY=0 NormalZ=1 AngleXU=0 Radius=4.25
    g1: Circle CenterX=-31 CenterY=-16 CenterZ=0 NormalX=0 NormalY=0 NormalZ=1 AngleXU=0 Radius=4.25
    g2: Circle CenterX=31 CenterY=-16 CenterZ=0 NormalX=0 NormalY=0 NormalZ=1 AngleXU=0 Radius=4.25
    g3: Circle CenterX=31 CenterY=16 CenterZ=0 NormalX=0 NormalY=0 NormalZ=1 AngleXU=0 Radius=4.25
    g4: Circle CenterX=11.1245 CenterY=78.6835 CenterZ=0 NormalX=0 NormalY=0 NormalZ=1 AngleXU=0 Radius=4.25
    g5: Circle CenterX=55.7372 CenterY=53.3051 CenterZ=0 NormalX=0 NormalY=0 NormalZ=1 AngleXU=0 Radius=4.25
    g6: LineSegment StartX=-5.79351 StartY=73.5299 StartZ=0 EndX=1.54536 EndY=84.0053 EndZ=0
    g7: LineSegment StartX=1.54536 StartY=84.0053 StartZ=0 EndX=19.0791 EndY=84.0053 EndZ=0
    g8: LineSegment StartX=19.0791 StartY=84.0053 StartZ=0 EndX=24.5689 EndY=73.5299 EndZ=0
    g9: LineSegment StartX=24.5689 StartY=73.5299 StartZ=0 EndX=-5.79351 EndY=73.5299 EndZ=0
    g10: LineSegment StartX=48.4901 StartY=42.1793 StartZ=0 EndX=65.9444 EndY=50.0388 EndZ=0
    g11: LineSegment StartX=65.9444 StartY=50.0388 StartZ=0 EndX=65.9444 EndY=68.6159 EndZ=0
    g12: LineSegment StartX=65.9444 StartY=68.6159 StartZ=0 EndX=48.4901 EndY=73.6175 EndZ=0
    g13: LineSegment StartX=48.4901 StartY=73.6175 StartZ=0 EndX=48.4901 EndY=42.1793 EndZ=0
  constraints (22):
    c: Equal(g3,g2)
    c: Equal(g2,g1)
    c: Equal(g1,g0)
    c: Symmetric(g1,g2,g-2)
    c: Symmetric(g0,g1,g-1)
    c: Symmetric(g2,g3,g-1)
    c: DistanceX(g-2,g3) = 31
    c: Distance(g2,g3) = 32
    c: Coincident(g6,g7)
    c: Horizontal(g7)
    c: Coincident(g7,g8)
    c: Coincident(g8,g9)
    c: Coincident(g9,g6)
    c: Horizontal(g9)
    c: Coincident(g10,g11)
    c: Vertical(g11)
    c: Coincident(g11,g12)
    c: Coincident(g12,g13)
    c: Coincident(g13,g10)
    c: Vertical(g13)
    c: Equal(g4,g5)
    c: Diameter(g4) = 8.5
FEATURE [PartDesign::Body] Body010  label="Hole sketching"
  AllowCompound = false
  Group = -> [Sketch020]
  Origin = -> Origin014
  Placement = pos=(24,0,0) rot=(0,0,1;0rad)
FEATURE [PartDesign::Chamfer] Chamfer012
  Angle = 45
  Base = -> Chamfer [Face22,Face1]
  BaseFeature = -> Chamfer
  ChamferType = 0
  FlipDirection = false
  Placement = pos=(0,0,0) rot=(1,1,1;2.0944rad)
  Refine = true
  Size = 0.6
  Size2 = 1
  SupportTransform = false
  Suppressed = false
  UseAllEdges = false
FEATURE [PartDesign::Body] Body002  label="Carriage body"
  AllowCompound = false
  Group = -> [Sketch003,Pad002,Sketch006,Pocket,Fillet006,Fillet007,Chamfer,Chamfer012]
  Origin = -> Origin006
  Tip = -> Chamfer012
FEATURE [Part::MultiFuse] Fusion
  Refine = true
  Shapes = -> [Clone015,Clone013,Clone014]
FEATURE [Part::Cut] Cut
  Base = -> Body002
  Refine = true
  Tool = -> Compound
FEATURE [Part::Cut] Cut001
  Base = -> Cut
  Refine = true
  Tool = -> Compound001
FEATURE [Part::Cut] Cut002  label="Bearing ring - with all booleans"
  Base = -> Cut001
  Refine = true
  Tool = -> Fusion
FEATURE [Part::FeaturePython] Screw  label="M8x1x40-Screw"  # WARN: FeaturePython — macro-defined, semantics opaque (R4)
  Diameter = 1
  Invert = false
  LeftHanded = false
  Length = 11
  LengthCustom = 40
  MatchOuter = false
  OffsetAngle = 0
  Placement = pos=(-5,-31,67.5) rot=(0,0,1;0rad)
  Thread = false
  Type = 42
  expr: .Placement.Base.x = <<Bearing001>>.Placement.Base.x
  expr: .Placement.Base.y = <<Bearing002>>.Placement.Base.y
FEATURE [App::Part] Part  label="Plain bearing ring and bearings"
  Group = -> [Part001,Screw,Body002,Clone006,Clone008,Clone009,Clone010,Clone011,Clone012,Compound,Compound001,Clone013,Clone014,Clone015,Fusion,Cut,Cut001,Cut002]
  Origin = -> Origin015
COMPONENT P1 — recipe-attached ("Steel tube", modeled in this document).
Construction recipe (the document's own serialized feature program — sketch geometry with constraints, then the solid features built on it; lengths are millimeters unless a unit is written):

FEATURE [Sketcher::SketchObject] Sketch  label="Master sketch for positions"
  ArcFitTolerance = 1e-06
  AttachmentSupport = -> [XZ_Plane]
  FullyConstrained = true
  MakeInternals = false
  MapMode = 5
  Placement = pos=(0,0,0) rot=(1,0,0;1.5708rad)
  expr: .Constraints.ring_edge = Fabricatable_Axis_6_01_60mmx40mm_tube_version_Bearing_ring#VarSet.Tube_height / 2 + Fabricatable_Axis_6_01_60mmx40mm_tube_version_Bearing_ring#VarSet.Bearing_od + Fabricatable_Axis_6_01_60mmx40mm_tube_version_Bearing_ring#VarSet.Carriage_to_bearing_top_clearance
  expr: Constraints[17] = Fabricatable_Axis_6_01_60mmx40mm_tube_version_Bearing_ring#VarSet.Tube_height / 2 + Fabricatable_Axis_6_01_60mmx40mm_tube_version_Bearing_ring#VarSet.Bearing_od / 2 + VarSet.Belt_bearing_to_tube_clearance * 1 mm
  sketch-geometry (8):
    g0: LineSegment StartX=-40.3051 StartY=53.5 StartZ=0 EndX=0 EndY=93.8051 EndZ=0
    g1: LineSegment StartX=0 StartY=93.8051 StartZ=0 EndX=40.3051 EndY=53.5 EndZ=0
    g2: LineSegment StartX=40.3051 StartY=53.5 StartZ=0 EndX=0 EndY=13.1949 EndZ=0
    g3: LineSegment StartX=0 StartY=13.1949 StartZ=0 EndX=-40.3051 EndY=53.5 EndZ=0
    g4: Circle CenterX=0 CenterY=53.5 CenterZ=0 NormalX=0 NormalY=0 NormalZ=1 AngleXU=0 Radius=6.75
    g5: Circle CenterX=20 CenterY=45 CenterZ=0 NormalX=0 NormalY=0 NormalZ=1 AngleXU=0 Radius=11
    g6: Circle CenterX=-20 CenterY=45 CenterZ=0 NormalX=0 NormalY=0 NormalZ=1 AngleXU=0 Radius=11
    g7: Circle CenterX=0 CenterY=53.5 CenterZ=0 NormalX=0 NormalY=0 NormalZ=1 AngleXU=0 Radius=9
  constraints (22):
    c: Coincident(g0,g1)
    c: Coincident(g1,g2)
    c: Coincident(g2,g3)
    c: Coincident(g3,g0)
    c: PointOnObject(g2,g-2)
    c: PointOnObject(g4,g-2)
    c: Symmetric(g2,g0,g4)
    c: Symmetric(g0,g1,g4)
    c: Angle(g2,g3) = 1.5708
    c: Distance(g0) = 57
    c: Equal(g1,g0)
    c: DistanceY(g-1,g2) = 13.1949
    c: Diameter(g5) = 22
    c: Equal(g6,g5)
    c: Symmetric(g6,g5,g-2)
    c: Diameter(g4) = 13.5
    c: DistanceY(g-1,g1) = 53.5  'ring_edge'
    c: DistanceY(g-1,g5) = 45
    c: Coincident(g7,g4)
    c: Diameter(g7) = 18
    c: Distance(g6,g5) = 40
    c: Distance(g1,g0) = 80.6102
FEATURE [PartDesign::SubShapeBinder] Binder
  BindCopyOnChange = 0
  BindMode = 0
  ClaimChildren = false
  Context = -> Body [Binder.]
  Fuse = false
  MakeFace = true
  OffsetFill = false
  OffsetIntersection = false
  OffsetJoinType = 0
  OffsetOpenResult = false
  PartialLoad = false
  Refine = true
  Relative = true
  Support = -> [Link002[Face1]]
  _Version = 2
FEATURE [PartDesign::Pad] Pad
  Direction = (-1,5.96046e-08,5.96046e-08)
  Length = 84
  Length2 = 10
  Midplane = true
  Profile = -> Binder
  Refine = true
  Suppressed = false
  Type = 0
  expr: Length = VarSet.Bearing_ring_spacing
FEATURE [Sketcher::SketchObject] Sketch001
  ArcFitTolerance = 1e-06
  AttachmentOffset = pos=(0,0,-26) rot=(0,0,1;0rad)
  AttachmentSupport = -> [XZ_Plane]
  ExternalGeometry = -> [Sketch]
  FullyConstrained = true
  MakeInternals = false
  MapMode = 5
  Placement = pos=(0,26,-5.8e-15) rot=(1,0,0;1.5708rad)
  expr: .AttachmentOffset.Base.z = Fabricatable_Axis_6_01_60mmx40mm_tube_version_Bearing_ring#VarSet.Tube_width / -2 - VarSet.Motor_distance_from_tube * 1 mm
  expr: Constraints[11] = 57 + 2 * 2
  sketch-geometry (5):
    g0: LineSegment StartX=43.1335 StartY=53.5 StartZ=0 EndX=0 EndY=96.6335 EndZ=0
    g1: LineSegment StartX=0 StartY=96.6335 StartZ=0 EndX=-43.1335 EndY=53.5 EndZ=0
    g2: LineSegment StartX=-43.1335 StartY=53.5 StartZ=0 EndX=7.1e-15 EndY=10.3665 EndZ=0
    g3: LineSegment StartX=7.1e-15 StartY=10.3665 StartZ=0 EndX=43.1335 EndY=53.5 EndZ=0
    g4: GeomPoint [constr] X=0 Y=53.5 Z=0
  constraints (12):
    c: Coincident(g0,g1)
    c: Coincident(g1,g2)
    c: Coincident(g2,g3)
    c: Coincident(g3,g0)
    c: Symmetric(g2,g0,g4)
    c: Equal(g1,g0)
    c: Angle(g1,g0) = 1.5708
    c: Equal(g3,g0)
    c: Equal(g3,g2)
    c: PointOnObject(g0,g-2)
    c: Coincident(g4,g-3)
    c: Distance(g3) = 61
FEATURE [PartDesign::Pocket] Pocket
  BaseFeature = -> Pad
  Direction = (0,1,-2e-16)
  Length = 5
  Length2 = 5
  Profile = -> Sketch001
  ReferenceAxis = -> Sketch001 [N_Axis]
  Refine = true
  Suppressed = false
  Type = 1
FEATURE [Sketcher::SketchObject] Sketch002
  ArcFitTolerance = 1e-06
  AttachmentOffset = pos=(0,0,-26) rot=(0,0,1;0rad)
  AttachmentSupport = -> [XZ_Plane]
  ExternalGeometry = -> [Sketch]
  FullyConstrained = true
  MakeInternals = false
  MapMode = 5
  Placement = pos=(0,26,-5.8e-15) rot=(1,0,0;1.5708rad)
  expr: .AttachmentOffset.Base.z = Fabricatable_Axis_6_01_60mmx40mm_tube_version_Bearing_ring#VarSet.Tube_width / -2 - VarSet.Motor_distance_from_tube * 1 mm
  sketch-geometry (3):
    g0: LineSegment StartX=0 StartY=93.8051 StartZ=0 EndX=-40.3051 EndY=53.5 EndZ=0
    g1: LineSegment StartX=-40.3051 StartY=53.5 StartZ=0 EndX=40.3051 EndY=53.5 EndZ=0
    g2: LineSegment StartX=40.3051 StartY=53.5 StartZ=0 EndX=0 EndY=93.8051 EndZ=0
  constraints (6):
    c: Coincident(g-4,g0)
    c: Coincident(g0,g-3)
    c: Coincident(g0,g1)
    c: Coincident(g1,g-4)
    c: Coincident(g1,g2)
    c: Coincident(g2,g0)
FEATURE [PartDesign::Pad] Pad001
  BaseFeature = -> Pocket
  Direction = (0,-1,2e-16)
  Length = 13
  Length2 = 10
  Profile = -> Sketch002
  ReferenceAxis = -> Sketch002 [N_Axis]
  Refine = true
  Suppressed = false
  Type = 0
  expr: Length = VarSet.Motor_support_wall_thickness
FEATURE [PartDesign::Chamfer] Chamfer  label="Chamfer001"
  Angle = 45
  Base = -> Pad001 [Edge77,Edge31]
  BaseFeature = -> Pad001
  ChamferType = 0
  FlipDirection = false
  Refine = true
  Size = 4
  Size2 = 1
  SupportTransform = false
  Suppressed = false
  UseAllEdges = false
FEATURE [PartDesign::Fillet] Fillet
  Base = -> Chamfer [Edge10,Edge14,Edge83,Edge85]
  BaseFeature = -> Chamfer
  Radius = 2
  Refine = true
  SupportTransform = false
  Suppressed = false
  UseAllEdges = false
FEATURE [PartDesign::Chamfer] Chamfer001  label="Chamfer002"
  Angle = 45
  Base = -> Fillet [Edge11,Edge15,Edge18,Edge39,Edge43,Edge8,Edge6,Edge4,Edge2,Edge1]
  BaseFeature = -> Fillet
  ChamferType = 0
  FlipDirection = false
  Refine = true
  Size = 0.6
  Size2 = 1
  SupportTransform = false
  Suppressed = false
  UseAllEdges = false
  expr: Size = Fabricatable_Axis_6_01_60mmx40mm_tube_version_Bearing_ring#Chamfer012.Size
FEATURE [Sketcher::SketchObject] Sketch003
  ArcFitTolerance = 1e-06
  AttachmentSupport = -> [XY_Plane]
  ExternalGeometry = -> [Sketch]
  FullyConstrained = true
  MakeInternals = false
  MapMode = 5
  expr: .Constraints.dist = Sketch002.Placement.Base.y - VarSet.Motor_support_wall_thickness * 1 mm
  expr: Constraints[13] = .Constraints.dist - Fabricatable_Axis_6_01_60mmx40mm_tube_version_Bearing_ring#VarSet.Bearing_width - Fabricatable_Axis_6_01_60mmx40mm_tube_version_Bearing_ring#VarSet.Bearing_washer_protrusion * 2
  sketch-geometry (5):
    g0: LineSegment StartX=-32 StartY=5.28 StartZ=0 EndX=32 EndY=5.28 EndZ=0
    g1: LineSegment StartX=32 StartY=5.28 StartZ=0 EndX=32 EndY=13 EndZ=0
    g2: LineSegment StartX=32 StartY=13 StartZ=0 EndX=-32 EndY=13 EndZ=0
    g3: LineSegment StartX=-32 StartY=13 StartZ=0 EndX=-32 EndY=5.28 EndZ=0
    g4: LineSegment [constr] StartX=-31 StartY=1e-14 StartZ=0 EndX=-32 EndY=1e-14 EndZ=0
  constraints (15):
    c: Coincident(g0,g1)
    c: Coincident(g1,g2)
    c: Coincident(g2,g3)
    c: Coincident(g3,g0)
    c: Horizontal(g0)
    c: Vertical(g1)
    c: Vertical(g3)
    c: Symmetric(g1,g2,g-2)
    c: DistanceY(g-1,g1) = 13  'dist'
    c: Coincident(g4,g-3)
    c: Angle(g4,g-1) = 3.14159
    c: Distance(g4) = 1
    c: PointOnObject(g4,g3)
    c: DistanceY(g-1,g0) = 5.28
    c: Distance(g1) = 7.72  'gapwidth'
FEATURE [PartDesign::Pocket] Pocket001
  BaseFeature = -> Chamfer001
  Direction = (0,0,-1)
  Length = 5
  Length2 = 5
  Profile = -> Sketch003
  ReferenceAxis = -> Sketch003 [N_Axis]
  Refine = true
  Reversed = true
  Suppressed = false
  Type = 1
FEATURE [Sketcher::SketchObject] Sketch004
  ArcFitTolerance = 1e-06
  AttachmentOffset = pos=(0,0,-13) rot=(0,0,1;0rad)
  AttachmentSupport = -> [XZ_Plane]
  ExternalGeometry = -> [Sketch]
  FullyConstrained = true
  MakeInternals = false
  MapMode = 5
  Placement = pos=(0,13,-2.9e-15) rot=(1,0,0;1.5708rad)
  expr: .AttachmentOffset.Base.z = -Sketch003.Constraints.dist
  expr: Constraints[21] = VarSet.Bearing_ring_spacing * 2
  sketch-geometry (10):
    g0: ArcOfCircle CenterX=0 CenterY=53.5 CenterZ=0 NormalX=0 NormalY=0 NormalZ=1 AngleXU=0 Radius=9.5 StartAngle=6.02735 EndAngle=9.68061
    g1: ArcOfCircle CenterX=-20 CenterY=45 CenterZ=0 NormalX=0 NormalY=0 NormalZ=1 AngleXU=0 Radius=12 StartAngle=4.71239 EndAngle=6.53902
    g2: ArcOfCircle CenterX=20 CenterY=45 CenterZ=0 NormalX=0 NormalY=0 NormalZ=1 AngleXU=0 Radius=12 StartAngle=2.88576 EndAngle=4.71239
    g3: LineSegment StartX=-9.1908 StartY=51.096 StartZ=0 EndX=-8.39057 EndY=48.0366 EndZ=0
    g4: LineSegment StartX=9.1908 StartY=51.096 StartZ=0 EndX=8.39057 EndY=48.0366 EndZ=0
    g5: LineSegment StartX=-20 StartY=33 StartZ=0 EndX=-84 EndY=33 EndZ=0
    g6: LineSegment StartX=-84 StartY=33 StartZ=0 EndX=-84 EndY=0 EndZ=0
    g7: LineSegment StartX=-84 StartY=0 StartZ=0 EndX=84 EndY=0 EndZ=0
    g8: LineSegment StartX=84 StartY=0 StartZ=0 EndX=84 EndY=33 EndZ=0
    g9: LineSegment StartX=84 StartY=33 StartZ=0 EndX=20 EndY=33 EndZ=0
  constraints (23):
    c: Coincident(g0,g-3)
    c: Diameter(g0) = 19
    c: Coincident(g1,g-4)
    c: Coincident(g2,g-5)
    c: Tangent(g4,g0) = 1.5708
    c: Tangent(g0,g3) = -1.5708
    c: Tangent(g3,g1) = 1.5708
    c: Tangent(g2,g4) = -1.5708
    c: Diameter(g2) = 24
    c: Equal(g1,g2)
    c: Horizontal(g5)
    c: Coincident(g5,g6)
    c: PointOnObject(g6,g-1)
    c: Coincident(g6,g7)
    c: Coincident(g7,g8)
    c: Vertical(g8)
    c: Coincident(g8,g9)
    c: Horizontal(g9)
    c: Tangent(g9,g2) = 1.5708
    c: Tangent(g1,g5) = 1.5708
    c: Symmetric(g6,g7,g-2)
    c: Distance(g7) = 168
    c: Vertical(g6)
FEATURE [Sketcher::SketchObject] Sketch005
  ArcFitTolerance = 1e-06
  AttachmentOffset = pos=(0,0,-14) rot=(0,0,1;0rad)
  AttachmentSupport = -> [XZ_Plane]
  ExternalGeometry = -> [Sketch]
  FullyConstrained = false
  MakeInternals = false
  MapMode = 5
  Placement = pos=(0,14,-3.1e-15) rot=(1,0,0;1.5708rad)
  expr: .AttachmentOffset.Base.z = -Sketch002.Placement.Base.y + VarSet.Motor_support_wall_thickness * 1 mm - 1 mm
  sketch-geometry (8):
    g0: LineSegment [constr] StartX=0 StartY=86.734 StartZ=0 EndX=-33.234 EndY=53.5 EndZ=0
    g1: LineSegment [constr] StartX=-33.234 StartY=53.5 StartZ=0 EndX=0 EndY=20.266 EndZ=0
    g2: LineSegment [constr] StartX=0 StartY=20.266 StartZ=0 EndX=33.234 EndY=53.5 EndZ=0
    g3: LineSegment [constr] StartX=33.234 StartY=53.5 StartZ=0 EndX=0 EndY=86.734 EndZ=0
    g4: Circle CenterX=-33.234 CenterY=53.5 CenterZ=0 NormalX=0 NormalY=0 NormalZ=1 AngleXU=0 Radius=2.3
    g5: Circle CenterX=0 CenterY=86.734 CenterZ=0 NormalX=0 NormalY=0 NormalZ=1 AngleXU=0 Radius=2.3
    g6: Circle CenterX=33.234 CenterY=53.5 CenterZ=0 NormalX=0 NormalY=0 NormalZ=1 AngleXU=0 Radius=2.3
    g7: Circle CenterX=0 CenterY=20.266 CenterZ=0 NormalX=0 NormalY=0 NormalZ=1 AngleXU=0 Radius=2.3
  constraints (16):
    c: PointOnObject(g0,g-2)
    c: Coincident(g0,g1)
    c: Coincident(g1,g2)
    c: Coincident(g2,g3)
    c: Coincident(g3,g0)
    c: Angle(g1,g0) = 1.5708
    c: Equal(g0,g3)
    c: Coincident(g4,g0)
    c: Coincident(g5,g0)
    c: Coincident(g6,g2)
    c: Coincident(g7,g1)
    c: Equal(g7,g6)
    c: Equal(g7,g5)
    c: Equal(g7,g4)
    c: Diameter(g7) = 4.6
    c: Distance(g0) = 47
FEATURE [Sketcher::SketchObject] Sketch006
  ArcFitTolerance = 1e-06
  AttachmentOffset = pos=(0,0,-5.28) rot=(0,0,1;0rad)
  AttachmentSupport = -> [XZ_Plane]
  ExternalGeometry = -> [Sketch]
  FullyConstrained = true
  MakeInternals = false
  MapMode = 5
  Placement = pos=(0,5.28,-1.2e-15) rot=(1,0,0;1.5708rad)
  expr: .AttachmentOffset.Base.z = -Sketch003.Constraints.dist + Sketch003.Constraints.gapwidth
  sketch-geometry (2):
    g0: Circle CenterX=-20 CenterY=45 CenterZ=0 NormalX=0 NormalY=0 NormalZ=1 AngleXU=0 Radius=4
    g1: Circle CenterX=20 CenterY=45 CenterZ=0 NormalX=0 NormalY=0 NormalZ=1 AngleXU=0 Radius=4
  constraints (4):
    c: Coincident(g0,g-3)
    c: Coincident(g1,g-4)
    c: Equal(g1,g0)
    c: Diameter(g1) = 8
FEATURE [Sketcher::SketchObject] Sketch007
  ArcFitTolerance = 1e-06
  AttachmentOffset = pos=(0,0,-5.28) rot=(0,0,1;0rad)
  AttachmentSupport = -> [XZ_Plane]
  ExternalGeometry = -> [Sketch]
  FullyConstrained = true
  MakeInternals = false
  MapMode = 5
  Placement = pos=(0,5.28,-1.2e-15) rot=(1,0,0;1.5708rad)
  expr: .AttachmentOffset.Base.z = -Sketch003.Constraints.dist + Sketch003.Constraints.gapwidth
  sketch-geometry (4):
    g0: Circle CenterX=-20 CenterY=45 CenterZ=0 NormalX=0 NormalY=0 NormalZ=1 AngleXU=0 Radius=4
    g1: Circle CenterX=20 CenterY=45 CenterZ=0 NormalX=0 NormalY=0 NormalZ=1 AngleXU=0 Radius=4
    g2: Circle CenterX=-20 CenterY=45 CenterZ=0 NormalX=0 NormalY=0 NormalZ=1 AngleXU=0 Radius=5.5
    g3: Circle CenterX=20 CenterY=45 CenterZ=0 NormalX=0 NormalY=0 NormalZ=1 AngleXU=0 Radius=5.5
  constraints (8):
    c: Coincident(g0,g-3)
    c: Coincident(g1,g-4)
    c: Coincident(g2,g0)
    c: Coincident(g3,g1)
    c: Equal(g1,g0)
    c: Diameter(g1) = 8
    c: Equal(g2,g3)
    c: Diameter(g2) = 11
FEATURE [Sketcher::SketchObject] Sketch008
  ArcFitTolerance = 1e-06
  AttachmentOffset = pos=(0,0,-13) rot=(0,0,1;0rad)
  AttachmentSupport = -> [XZ_Plane]
  ExternalGeometry = -> [Sketch]
  FullyConstrained = false
  MakeInternals = false
  MapMode = 5
  Placement = pos=(0,13,-2.9e-15) rot=(1,0,0;1.5708rad)
  expr: .AttachmentOffset.Base.z = -Sketch003.Constraints.dist
  sketch-geometry (9):
    g0: ArcOfCircle CenterX=-20 CenterY=45 CenterZ=0 NormalX=0 NormalY=0 NormalZ=1 AngleXU=0 Radius=10 StartAngle=2.4251 EndAngle=4.66182
    g1: ArcOfCircle CenterX=0 CenterY=53.5 CenterZ=0 NormalX=0 NormalY=0 NormalZ=1 AngleXU=0 Radius=19.5 StartAngle=0.71649 EndAngle=2.4251
    g2: ArcOfCircle CenterX=20 CenterY=45 CenterZ=0 NormalX=0 NormalY=0 NormalZ=1 AngleXU=0 Radius=10 StartAngle=4.76295 EndAngle=6.99968
    g3: LineSegment StartX=-27.5412 StartY=51.5674 StartZ=0 EndX=-14.7052 EndY=66.3065 EndZ=0
    g4: LineSegment StartX=14.7052 StartY=66.3065 StartZ=0 EndX=27.5412 EndY=51.5674 EndZ=0
    g5: Circle [constr] CenterX=0 CenterY=53.5 CenterZ=0 NormalX=0 NormalY=0 NormalZ=1 AngleXU=0 Radius=16.3644
    g6: ArcOfCircle CenterX=0 CenterY=53.5 CenterZ=0 NormalX=0 NormalY=0 NormalZ=1 AngleXU=0 Radius=19.5 StartAngle=4.66182 EndAngle=4.76295
    g7: LineSegment StartX=-20.5054 StartY=35.0128 StartZ=0 EndX=-0.985592 EndY=34.0249 EndZ=0
    g8: LineSegment StartX=20.5054 StartY=35.0128 StartZ=0 EndX=0.985592 EndY=34.0249 EndZ=0
  constraints (18):
    c: Coincident(g0,g-3)
    c: Coincident(g1,g-4)
    c: Coincident(g2,g-5)
    c: Tangent(g2,g4) = 1.5708
    c: Tangent(g4,g1) = 1.5708
    c: Tangent(g1,g3) = 1.5708
    c: Tangent(g3,g0) = 1.5708
    c: Diameter(g1) = 39
    c: Equal(g0,g2)
    c: Diameter(g0) = 20
    c: Coincident(g5,g1)
    c: Diameter(g5) = 32.7287
    c: Coincident(g6,g1)
    c: Equal(g6,g1)
    c: Tangent(g8,g2) = 1.5708
    c: Tangent(g8,g6) = 1.5708
    c: Tangent(g6,g7) = -1.5708
    c: Tangent(g7,g0) = -1.5708
FEATURE [PartDesign::Pocket] Pocket003
  BaseFeature = -> Pocket001
  Direction = (0,1,-2e-16)
  Length = 5
  Length2 = 5
  Profile = -> Sketch008
  ReferenceAxis = -> Sketch008 [N_Axis]
  Refine = true
  Suppressed = false
  Type = 1
FEATURE [PartDesign::Pocket] Pocket002
  BaseFeature = -> Pocket003
  Direction = (0,1,-2e-16)
  Length = 13.72
  Length2 = 3
  Profile = -> Sketch004
  ReferenceAxis = -> Sketch004 [N_Axis]
  Refine = true
  Reversed = true
  Suppressed = false
  Type = 0
  expr: Length = Sketch003.Constraints.gapwidth + 6 mm
FEATURE [PartDesign::Chamfer] Chamfer002  label="Chamfer003"
  Angle = 45
  Base = -> Pocket002 [Edge206,Edge198]
  BaseFeature = -> Pocket002
  ChamferType = 0
  FlipDirection = false
  Refine = true
  Size = 5.9
  Size2 = 1
  SupportTransform = false
  Suppressed = false
  UseAllEdges = false
FEATURE [PartDesign::Pad] Pad002
  BaseFeature = -> Chamfer002
  Direction = (0,-1,2e-16)
  Length = 0.36
  Length2 = 10
  Profile = -> Sketch007
  ReferenceAxis = -> Sketch007 [N_Axis]
  Refine = true
  Reversed = true
  Suppressed = false
  Type = 0
  expr: Length = Fabricatable_Axis_6_01_60mmx40mm_tube_version_Bearing_ring#VarSet.Bearing_washer_protrusion
FEATURE [PartDesign::Hole] Hole
  BaseFeature = -> Pad002
  CustomThreadClearance = 0
  Depth = 25
  DepthType = 0
  Diameter = 7.7
  DrillForDepth = false
  DrillPoint = 1
  DrillPointAngle = 118
  HoleCutCountersinkAngle = 90
  HoleCutCustomValues = false
  HoleCutDepth = 0
  HoleCutDiameter = 6.1
  HoleCutType = 0
  ModelThread = false
  Profile = -> Sketch006
  Refine = true
  Reversed = true
  Suppressed = false
  Tapered = false
  TaperedAngle = 90
  ThreadClass = 0
  ThreadDepth = 25
  ThreadDepthType = 0
  ThreadDirection = 0
  ThreadFit = 0
  ThreadSize = 0
  ThreadType = 0
  Threaded = false
  UseCustomThreadClearance = false
  expr: Diameter = Fabricatable_Axis_6_01_60mmx40mm_tube_version_Bearing_ring#VarSet.Bearing_axle_screw_selftap_diameter
FEATURE [PartDesign::Pocket] Pocket004
  BaseFeature = -> Hole
  Direction = (0,1,-2e-16)
  Length = 5
  Length2 = 5
  Profile = -> Sketch005
  ReferenceAxis = -> Sketch005 [N_Axis]
  Refine = true
  Suppressed = false
  Type = 1
FEATURE [PartDesign::Chamfer] Chamfer003  label="Chamfer004"
  Angle = 45
  Base = -> Pocket004 [Edge73,Edge74,Edge72,Edge233]
  BaseFeature = -> Pocket004
  ChamferType = 0
  FlipDirection = false
  Refine = true
  Size = 0.8
  Size2 = 1
  SupportTransform = false
  Suppressed = false
  UseAllEdges = false
FEATURE [Sketcher::SketchObject] Sketch009
  ArcFitTolerance = 1e-06
  AttachmentOffset = pos=(0,0,43.5) rot=(0,0,1;0rad)
  AttachmentSupport = -> [XZ_Plane]
  FullyConstrained = false
  MakeInternals = false
  MapMode = 5
  Placement = pos=(0,-43.5,9.7e-15) rot=(1,0,0;1.5708rad)
  expr: .AttachmentOffset.Base.z = Fabricatable_Axis_6_01_60mmx40mm_tube_version_Bearing_ring#VarSet.Tube_width / 2 + Fabricatable_Axis_6_01_60mmx40mm_tube_version_Bearing_ring#VarSet.Bearing_od + Fabricatable_Axis_6_01_60mmx40mm_tube_version_Bearing_ring#VarSet.Carriage_to_bearing_top_clearance
  sketch-geometry (1):
    g0: Circle CenterX=-37.5 CenterY=-37.5 CenterZ=0 NormalX=0 NormalY=0 NormalZ=1 AngleXU=0 Radius=1.65249
  constraints (2):
    c: DistanceX(g-2,g0) = -37.5
    c: DistanceY(g-1,g0) = -37.5
FEATURE [PartDesign::Hole] Hole001
  BaseFeature = -> Chamfer003
  CustomThreadClearance = 0
  Depth = 18
  DepthType = 0
  Diameter = 4.6
  DrillForDepth = false
  DrillPoint = 1
  DrillPointAngle = 118
  HoleCutCountersinkAngle = 90
  HoleCutCustomValues = false
  HoleCutDepth = 0
  HoleCutDiameter = 6.1
  HoleCutType = 2
  ModelThread = false
  Profile = -> Sketch009
  Refine = true
  Suppressed = false
  Tapered = false
  TaperedAngle = 90
  ThreadClass = 0
  ThreadDepth = 18
  ThreadDepthType = 0
  ThreadDirection = 0
  ThreadFit = 0
  ThreadSize = 0
  ThreadType = 0
  Threaded = false
  UseCustomThreadClearance = false
FEATURE [PartDesign::LinearPattern] LinearPattern
  Direction = -> X_Axis
  Length = 75
  Mode = 1
  Occurrences = 4
  Offset = 25
  Refine = true
  Suppressed = false
  TransformMode = 0
FEATURE [PartDesign::LinearPattern] LinearPattern001
  Direction = -> Z_Axis
  Length = 75
  Mode = 1
  Occurrences = 4
  Offset = 25
  Refine = true
  Suppressed = false
  TransformMode = 0
FEATURE [PartDesign::MultiTransform] MultiTransform
  BaseFeature = -> Hole001
  Originals = -> [Hole001]
  Refine = true
  Suppressed = false
  TransformMode = 0
  Transformations = -> [LinearPattern,LinearPattern001]
FEATURE [PartDesign::Body] Body  label="Connecting body"
  AllowCompound = false
  Group = -> [Sketch,Binder,Pad,Sketch001,Pocket,Sketch002,Pad001,Chamfer,Fillet,Chamfer001,Sketch003,Pocket001,Pocket003,Sketch004,Pocket002,Chamfer002,Sketch005,Sketch006,Sketch007,Pad002,Hole,Sketch008,Pocket004,Chamfer003,Sketch009,Hole001,MultiTransform,LinearPattern,LinearPattern001]
  Origin = -> Origin
  Tip = -> MultiTransform
COMPONENT P2 — geometry summary ("Chamfer"; no construction recipe available for this part):
  bounding box: 107.0 x 87.0 x 48.0 mm
  tessellated surface: 688 triangles
  volume: 312104 mm^3 (70% of its bounding box)
  symmetry: mirror-symmetric across its x mid-plane
COMPONENT P3 — geometry summary ("Carriage - oriented for print"; no construction recipe available for this part):
  bounding box: 178.0 x 144.5 x 87.0 mm
  tessellated surface: 89,706 triangles
  volume: 1004736 mm^3 (45% of its bounding box)
  symmetry: mirror-symmetric across its z mid-plane
PROVENANCE & LICENSES
A FreeCAD (.FCStd) document from a public repository crawl; recipes are the document's own serialized feature recipes (and, for linked parts, companion documents' recipes).
License: as declared in the source repository (recorded in the dataset sidecar).
